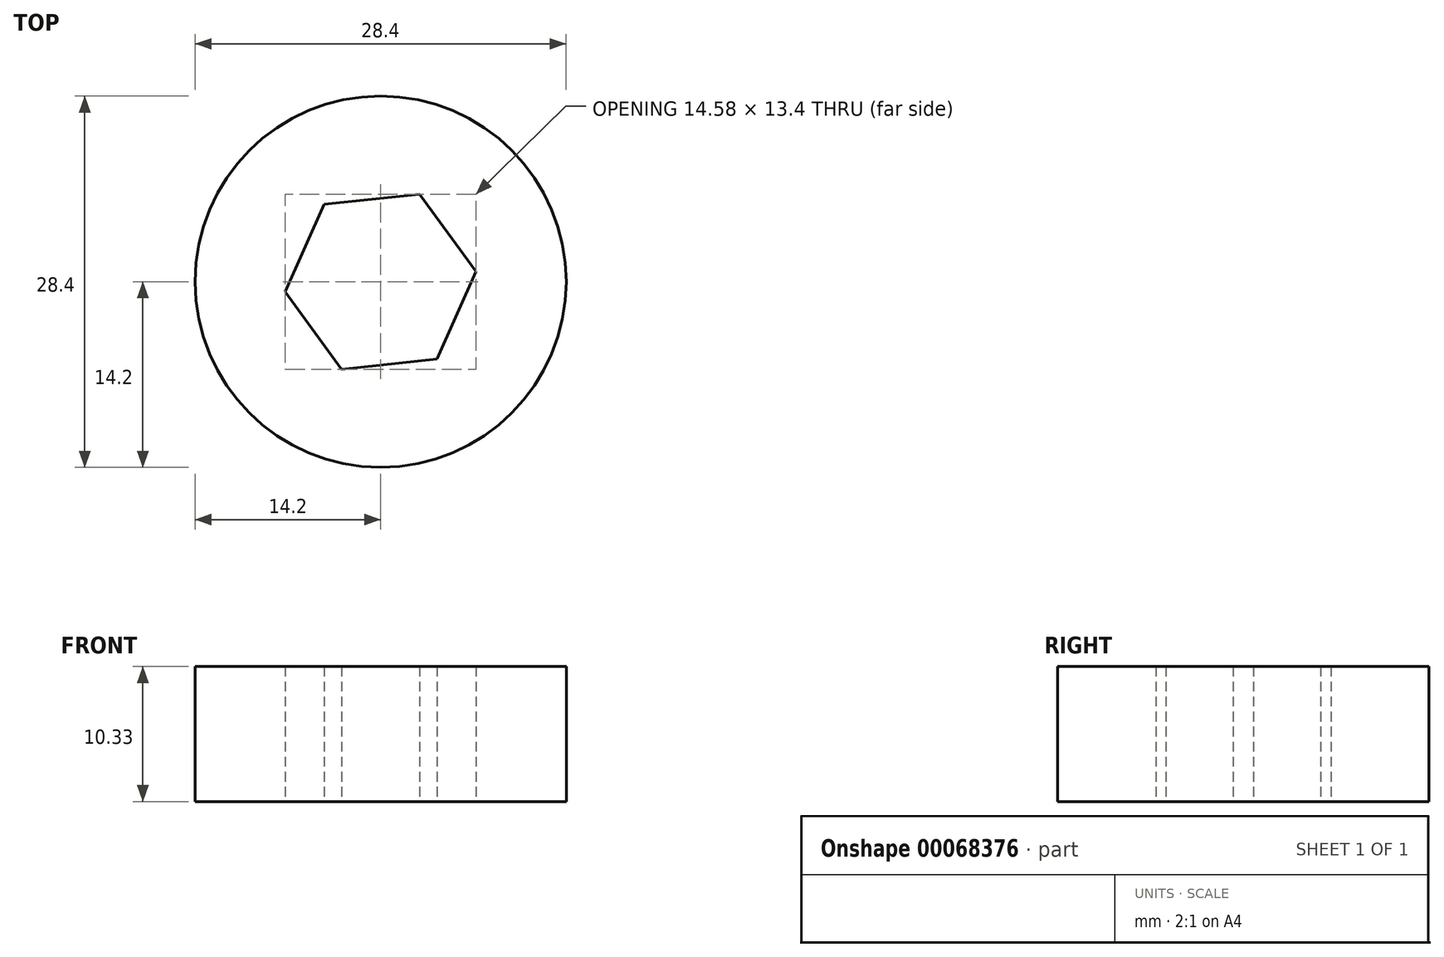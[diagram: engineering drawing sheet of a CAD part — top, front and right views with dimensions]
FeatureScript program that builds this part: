
annotation { "Feature Type Name" : "Feature", "Feature Type Description" : "" }
export const myFeature = defineFeature(function(context is Context, id is Id, definition is map)
    precondition{}
    {
        {
            var Q0;
            Q0=qCreatedBy(makeId("Top.planeOp"),FACE);
            var sketch = newSketch(context, id + "F0", { "sketchPlane" : qUnion([Q0])});
            skCircle(sketch, "E0", {"center": v(0, 0) * mm, "radius": 14.2 * mm});
            skCircle(sketch, "E1.cCircle", {"center": v(0, 0) * mm, "radius": 6.35 * mm, "construction": true});
            skLineSegment(sketch, "E1.0", {"start": v(7.3, 0.78) * mm, "end": v(4.32, -5.93) * mm});
            skLineSegment(sketch, "E1.1", {"start": v(4.32, -5.93) * mm, "end": v(-2.97, -6.7) * mm});
            skLineSegment(sketch, "E1.2", {"start": v(-2.97, -6.7) * mm, "end": v(-7.3, -0.78) * mm});
            skLineSegment(sketch, "E1.3", {"start": v(-7.3, -0.78) * mm, "end": v(-4.32, 5.93) * mm});
            skLineSegment(sketch, "E1.4", {"start": v(-4.32, 5.93) * mm, "end": v(2.97, 6.7) * mm});
            skLineSegment(sketch, "E1.5", {"start": v(2.97, 6.7) * mm, "end": v(7.3, 0.78) * mm});
            skPoint(sketch, "E1.0.midPoint", {"position": v(5.8, -2.58) * mm});
            skSolve(sketch);
        }
        {
            var Q0;
            Q0 = qSketchRegion(id + "F0", true);
            extrude(context, id + "F1", {"entities" : qUnion([Q0]), "depth" : 10.33 * mm});
        }
    });
